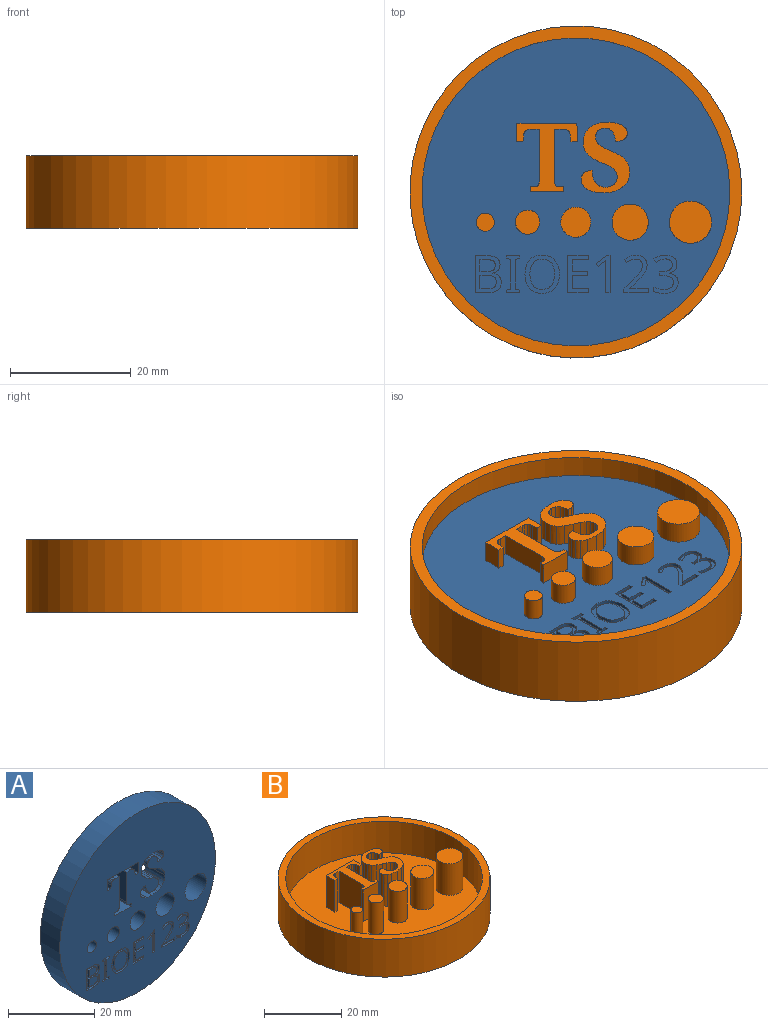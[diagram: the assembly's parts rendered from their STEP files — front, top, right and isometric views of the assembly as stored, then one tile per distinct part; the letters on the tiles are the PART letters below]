
ASSEMBLY  parts=2 mates=1
PART A: 230 faces, bbox 51x6.4x51 mm
  f0: plane 51x51mm, normal (0,-1,0), area 1751.3mm2, adj f2,f3,f4,f5,f6,f7,f8,f9
  f1: plane 51x51mm, normal (0,1,0), area 1845.5mm2, adj f2,f3,f4,f5,f6,f7,f8,f9
  f2: cylinder r=25.5mm len=51mm, axis (0,1,0), area 1017.4mm2, adj f0,f1
  f3: plane 8.53x6.35mm, normal (-1,0,0), area 54.2mm2, adj f0,f1,f4,f34
  f4: plane 6.35x1.28mm, normal (0,0,1), area 8.1mm2, adj f0,f1,f3,f5
  f5: extruded ~6.35x0.6mm, area 3.9mm2, adj f0,f1,f4,f6
  f6: extruded ~6.35x0.39mm, area 2.9mm2, adj f0,f1,f5,f7
  f7: extruded ~6.35x0.36mm, area 2.7mm2, adj f0,f1,f6,f8
  f8: extruded ~6.35x0.48mm, area 3.1mm2, adj f0,f1,f7,f9
  f9: plane 6.35x0.99mm, normal (0.99,0,0.12), area 6.3mm2, adj f0,f1,f8,f10
  f10: plane 6.35x1.07mm, normal (0,0,1), area 6.8mm2, adj f0,f1,f9,f11
  f11: plane 6.35x3.09mm, normal (-1,0,-0.03), area 19.6mm2, adj f0,f1,f10,f12
  f12: plane 9.94x6.35mm, normal (0,0,-1), area 63.1mm2, adj f0,f1,f11,f13
  f13: plane 6.35x3.09mm, normal (1,0,-0.03), area 19.6mm2, adj f0,f1,f12,f14
  f14: plane 6.35x1.07mm, normal (0,0,1), area 6.8mm2, adj f0,f1,f13,f15
  f15: plane 6.35x0.99mm, normal (-0.99,0,0.11), area 6.3mm2, adj f0,f1,f14,f16
  f16: extruded ~6.35x0.48mm, area 3.1mm2, adj f0,f1,f15,f17
  f17: extruded ~6.35x0.36mm, area 2.7mm2, adj f0,f1,f16,f18
  f18: extruded ~6.35x0.39mm, area 2.9mm2, adj f0,f1,f17,f19
  f19: extruded ~6.35x0.6mm, area 3.9mm2, adj f0,f1,f18,f20
  f20: plane 6.35x1.28mm, normal (0,0,1), area 8.1mm2, adj f0,f1,f19,f21
  f21: plane 8.53x6.35mm, normal (1,0,0), area 54.2mm2, adj f0,f1,f20,f22
  f22: extruded ~6.35x0.54mm, area 3.5mm2, adj f0,f1,f21,f23
  f23: extruded ~6.35x0.31mm, area 2.3mm2, adj f0,f1,f22,f24
  f24: extruded ~6.35x0.26mm, area 1.9mm2, adj f0,f1,f23,f25
  f25: extruded ~6.35x0.33mm, area 2.1mm2, adj f0,f1,f24,f26
  f26: plane 6.35x0.67mm, normal (0,0,-1), area 4.3mm2, adj f0,f1,f25,f27
  f27: plane 6.35x0.85mm, normal (1,0,0), area 5.4mm2, adj f0,f1,f26,f28
  f28: plane 6.35x5.51mm, normal (0,0,1), area 35mm2, adj f0,f1,f27,f29
  f29: plane 6.35x0.85mm, normal (-1,0,0), area 5.4mm2, adj f0,f1,f28,f30
  f30: plane 6.35x0.67mm, normal (0,0,-1), area 4.3mm2, adj f0,f1,f29,f31
  f31: extruded ~6.35x0.32mm, area 2mm2, adj f0,f1,f30,f32
  f32: extruded ~6.35x0.26mm, area 1.9mm2, adj f0,f1,f31,f33
  f33: extruded ~6.35x0.31mm, area 2.3mm2, adj f0,f1,f32,f34
  f34: extruded ~6.35x0.54mm, area 3.5mm2, adj f0,f1,f3,f33
  f35: extruded ~6.35x1.79mm, area 11.6mm2, adj f0,f1,f36,f90
  f36: extruded ~6.35x1.37mm, area 9.9mm2, adj f0,f1,f35,f37
  f37: extruded ~6.35x1.1mm, area 9mm2, adj f0,f1,f36,f38
  f38: extruded ~6.35x1.41mm, area 9.3mm2, adj f0,f1,f37,f39
  f39: extruded ~6.35x1.06mm, area 6.9mm2, adj f0,f1,f38,f40
  f40: extruded ~6.35x0.88mm, area 6.6mm2, adj f0,f1,f39,f41
  f41: extruded ~6.35x0.95mm, area 7.7mm2, adj f0,f1,f40,f42
  f42: extruded ~6.35x1.4mm, area 9.9mm2, adj f0,f1,f41,f43
  f43: extruded ~6.35x1.32mm, area 9.2mm2, adj f0,f1,f42,f44
  f44: extruded ~6.35x0.8mm, area 6.3mm2, adj f0,f1,f43,f45
  f45: extruded ~6.35x0.58mm, area 4.5mm2, adj f0,f1,f44,f46
  f46: extruded ~6.35x0.63mm, area 4.1mm2, adj f0,f1,f45,f47
  f47: extruded ~6.35x0.64mm, area 4.1mm2, adj f0,f1,f46,f48
  f48: extruded ~6.35x0.46mm, area 3.7mm2, adj f0,f1,f47,f49
  f49: extruded ~6.35x0.5mm, area 3.7mm2, adj f0,f1,f48,f50
  f50: extruded ~6.35x0.61mm, area 3.9mm2, adj f0,f1,f49,f51
  f51: extruded ~6.35x0.78mm, area 5.2mm2, adj f0,f1,f50,f52
  f52: extruded ~6.35x0.55mm, area 4.9mm2, adj f0,f1,f51,f53
  f53: extruded ~6.35x0.72mm, area 4.9mm2, adj f0,f1,f52,f54
  f54: extruded ~6.35x0.72mm, area 4.6mm2, adj f0,f1,f53,f55
  f55: extruded ~6.35x0.86mm, area 5.5mm2, adj f0,f1,f54,f56
  f56: extruded ~6.35x0.62mm, area 4.3mm2, adj f0,f1,f55,f57
  f57: extruded ~6.35x0.42mm, area 3.6mm2, adj f0,f1,f56,f58
  f58: extruded ~6.35x0.52mm, area 3.4mm2, adj f0,f1,f57,f59
  f59: extruded ~6.35x0.73mm, area 4.9mm2, adj f0,f1,f58,f60
  f60: extruded ~6.35x0.62mm, area 5.5mm2, adj f0,f1,f59,f61
  f61: extruded ~6.35x1.06mm, area 7.2mm2, adj f0,f1,f60,f62
  f62: extruded ~6.35x1.52mm, area 9.7mm2, adj f0,f1,f61,f63
  f63: extruded ~6.35x1.56mm, area 10mm2, adj f0,f1,f62,f64
  f64: extruded ~6.35x1.24mm, area 8.9mm2, adj f0,f1,f63,f65
  f65: extruded ~6.35x1.01mm, area 8.3mm2, adj f0,f1,f64,f66
  f66: extruded ~6.35x1.32mm, area 8.7mm2, adj f0,f1,f65,f67
  f67: extruded ~6.35x1.07mm, area 6.9mm2, adj f0,f1,f66,f68
  f68: extruded ~6.35x0.91mm, area 6.7mm2, adj f0,f1,f67,f69
  f69: extruded ~6.35x0.92mm, area 7.7mm2, adj f0,f1,f68,f70
  f70: extruded ~6.35x1.41mm, area 10mm2, adj f0,f1,f69,f71
  f71: extruded ~6.35x1.17mm, area 8.2mm2, adj f0,f1,f70,f72
  f72: extruded ~6.35x0.83mm, area 6.2mm2, adj f0,f1,f71,f73
  f73: extruded ~6.35x0.58mm, area 4.9mm2, adj f0,f1,f72,f74
  f74: extruded ~6.35x0.72mm, area 4.7mm2, adj f0,f1,f73,f75
  f75: extruded ~6.35x0.68mm, area 4.4mm2, adj f0,f1,f74,f76
  f76: extruded ~6.35x0.55mm, area 4.3mm2, adj f0,f1,f75,f77
  f77: extruded ~6.35x0.62mm, area 4.6mm2, adj f0,f1,f76,f78
  f78: extruded ~6.35x0.83mm, area 5.4mm2, adj f0,f1,f77,f79
  f79: extruded ~6.35x0.88mm, area 5.7mm2, adj f0,f1,f78,f80
  f80: extruded ~6.35x0.69mm, area 5.5mm2, adj f0,f1,f79,f81
  f81: extruded ~6.35x0.87mm, area 6.2mm2, adj f0,f1,f80,f82
  f82: extruded ~6.35x1.2mm, area 7.7mm2, adj f0,f1,f81,f83
  f83: extruded ~6.35x0.67mm, area 4.3mm2, adj f0,f1,f82,f84
  f84: extruded ~6.35x0.58mm, area 4mm2, adj f0,f1,f83,f85
  f85: extruded ~6.35x0.46mm, area 3.9mm2, adj f0,f1,f84,f86
  f86: extruded ~6.35x0.69mm, area 4.6mm2, adj f0,f1,f85,f87
  f87: extruded ~6.35x0.79mm, area 5.2mm2, adj f0,f1,f86,f88
  f88: extruded ~6.35x0.72mm, area 6.1mm2, adj f0,f1,f87,f89
  f89: extruded ~6.35x1.15mm, area 8mm2, adj f0,f1,f88,f90
  f90: extruded ~6.35x1.79mm, area 11.5mm2, adj f0,f1,f35,f89
  f91: cylinder r=3.5mm len=7mm, axis (0,-1,0), area 139.6mm2, adj f0,f1
  f92: cylinder r=3mm len=6.35mm, axis (0,-1,0), area 119.7mm2, adj f0,f1
  f93: cylinder r=1.5mm len=6.35mm, axis (0,-1,0), area 59.8mm2, adj f0,f1
  f94: cylinder r=2mm len=6.35mm, axis (0,-1,0), area 79.8mm2, adj f0,f1
  f95: cylinder r=2.5mm len=6.35mm, axis (0,-1,0), area 99.7mm2, adj f0,f1
  f96: plane 0.5x0.45mm, normal (-1,0,0), area 0.2mm2, adj f0,f97,f107,f108
  f97: plane 0.73x0.5mm, normal (-0.22,0,-0.98), area 0.4mm2, adj f0,f96,f98,f108
  f98: plane 4.94x0.5mm, normal (-1,0,0), area 2.5mm2, adj f0,f97,f99,f108
  f99: plane 0.73x0.5mm, normal (-0.23,0,0.97), area 0.4mm2, adj f0,f98,f100,f108
  f100: plane 0.5x0.45mm, normal (-1,0,0), area 0.2mm2, adj f0,f99,f101,f108
  f101: plane 2.23x0.5mm, normal (0,0,-1), area 1.1mm2, adj f0,f100,f102,f108
  f102: plane 0.5x0.45mm, normal (1,0,0), area 0.2mm2, adj f0,f101,f103,f108
  f103: plane 0.73x0.5mm, normal (0.23,0,0.97), area 0.4mm2, adj f0,f102,f104,f108
  f104: plane 4.94x0.5mm, normal (1,0,0), area 2.5mm2, adj f0,f103,f105,f108
  f105: plane 0.73x0.5mm, normal (0.22,0,-0.98), area 0.4mm2, adj f0,f104,f106,f108
  f106: plane 0.5x0.45mm, normal (1,0,0), area 0.2mm2, adj f0,f105,f107,f108
  f107: plane 2.23x0.5mm, normal (0,0,1), area 1.1mm2, adj f0,f96,f106,f108
  f108: plane 6.17x2.23mm, normal (0,-1,0), area 6.3mm2, adj f96,f97,f98,f99,f100,f101,f102,f103
  f109: plane 0.68x0.5mm, normal (-1,0,0), area 0.3mm2, adj f0,f110,f120,f121
  f110: plane 2.67x0.5mm, normal (0,0,-1), area 1.3mm2, adj f0,f109,f111,f121
  f111: plane 2.2x0.5mm, normal (-1,0,0), area 1.1mm2, adj f0,f110,f112,f121
  f112: plane 2.52x0.5mm, normal (0,0,1), area 1.3mm2, adj f0,f111,f113,f121
  f113: plane 0.68x0.5mm, normal (-1,0,0), area 0.3mm2, adj f0,f112,f114,f121
  f114: plane 2.52x0.5mm, normal (0,0,-1), area 1.3mm2, adj f0,f113,f115,f121
  f115: plane 1.92x0.5mm, normal (-1,0,0), area 1mm2, adj f0,f114,f116,f121
  f116: plane 2.67x0.5mm, normal (0,0,1), area 1.3mm2, adj f0,f115,f117,f121
  f117: plane 0.68x0.5mm, normal (-1,0,0), area 0.3mm2, adj f0,f116,f118,f121
  f118: plane 3.45x0.5mm, normal (0,0,-1), area 1.7mm2, adj f0,f117,f119,f121
  f119: plane 6.17x0.5mm, normal (1,0,0), area 3.1mm2, adj f0,f118,f120,f121
  f120: plane 3.45x0.5mm, normal (0,0,1), area 1.7mm2, adj f0,f109,f119,f121
  f121: plane 6.17x3.45mm, normal (0,-1,0), area 10.1mm2, adj f109,f110,f111,f112,f113,f114,f115,f116
  f122: plane 6.17x0.5mm, normal (-1,0,0), area 3.1mm2, adj f0,f123,f130,f131
  f123: plane 0.63x0.5mm, normal (0,0,-1), area 0.3mm2, adj f0,f122,f124,f131
  f124: plane 1.67x1.3mm, normal (0.61,0,-0.79), area 1.1mm2, adj f0,f123,f125,f131
  f125: plane 0.51x0.5mm, normal (0.79,0,0.61), area 0.3mm2, adj f0,f124,f126,f131
  f126: extruded ~0.94x0.78mm, area 0.6mm2, adj f0,f125,f127,f131
  f127: extruded ~0.5x0.25mm, area 0.2mm2, adj f0,f126,f128,f131
  f128: extruded ~1.06x0.5mm, area 0.5mm2, adj f0,f127,f129,f131
  f129: plane 4.31x0.5mm, normal (1,0,0), area 2.2mm2, adj f0,f128,f130,f131
  f130: plane 0.74x0.5mm, normal (0,0,1), area 0.4mm2, adj f0,f122,f129,f131
  f131: plane 6.17x2.3mm, normal (0,-1,0), area 5.6mm2, adj f122,f123,f124,f125,f126,f127,f128,f129
  f132: plane 0.69x0.5mm, normal (-1,0,0), area 0.3mm2, adj f0,f133,f152,f153
  f133: plane 3.12x0.5mm, normal (0,0,-1), area 1.6mm2, adj f0,f132,f134,f153
  f134: plane 0.5x0.03mm, normal (-1,0,0), area 0mm2, adj f0,f133,f135,f153
  f135: plane 1.29x1.27mm, normal (-0.7,0,0.71), area 0.9mm2, adj f0,f134,f136,f153
  f136: extruded ~1.07x0.99mm, area 0.7mm2, adj f0,f135,f137,f153
  f137: extruded ~0.77x0.5mm, area 0.4mm2, adj f0,f136,f138,f153
  f138: extruded ~0.78x0.5mm, area 0.4mm2, adj f0,f137,f139,f153
  f139: extruded ~1.2x0.5mm, area 0.7mm2, adj f0,f138,f140,f153
  f140: extruded ~1.37x0.5mm, area 0.7mm2, adj f0,f139,f141,f153
  f141: extruded ~1.89x0.73mm, area 1mm2, adj f0,f140,f142,f153
  f142: plane 0.51x0.5mm, normal (0.78,0,0.62), area 0.3mm2, adj f0,f141,f143,f153
  f143: extruded ~0.77x0.5mm, area 0.4mm2, adj f0,f142,f144,f153
  f144: extruded ~0.72x0.5mm, area 0.4mm2, adj f0,f143,f145,f153
  f145: extruded ~0.8x0.5mm, area 0.4mm2, adj f0,f144,f146,f153
  f146: extruded ~0.76x0.5mm, area 0.4mm2, adj f0,f145,f147,f153
  f147: extruded ~0.64x0.5mm, area 0.3mm2, adj f0,f146,f148,f153
  f148: extruded ~0.61x0.5mm, area 0.4mm2, adj f0,f147,f149,f153
  f149: extruded ~1.06x0.97mm, area 0.7mm2, adj f0,f148,f150,f153
  f150: plane 1.63x1.62mm, normal (0.71,0,-0.7), area 1.1mm2, adj f0,f149,f151,f153
  f151: plane 0.63x0.5mm, normal (1,0,0), area 0.3mm2, adj f0,f150,f152,f153
  f152: plane 4.08x0.5mm, normal (0,0,1), area 2mm2, adj f0,f132,f151,f153
  f153: plane 6.26x4.08mm, normal (0,-1,0), area 9mm2, adj f132,f133,f134,f135,f136,f137,f138,f139
  f154: extruded ~1.12x0.5mm, area 0.6mm2, adj f0,f155,f181,f182
  f155: extruded ~1.41x0.5mm, area 0.7mm2, adj f0,f154,f156,f182
  f156: extruded ~1.05x0.5mm, area 0.5mm2, adj f0,f155,f157,f182
  f157: extruded ~0.88x0.5mm, area 0.5mm2, adj f0,f156,f158,f182
  f158: plane 0.52x0.5mm, normal (0.81,0,0.59), area 0.3mm2, adj f0,f157,f159,f182
  f159: extruded ~0.8x0.5mm, area 0.4mm2, adj f0,f158,f160,f182
  f160: extruded ~0.76x0.5mm, area 0.4mm2, adj f0,f159,f161,f182
  f161: extruded ~0.83x0.5mm, area 0.4mm2, adj f0,f160,f162,f182
  f162: extruded ~0.69x0.5mm, area 0.4mm2, adj f0,f161,f163,f182
  f163: extruded ~0.86x0.5mm, area 0.5mm2, adj f0,f162,f164,f182
  f164: extruded ~1.14x0.5mm, area 0.6mm2, adj f0,f163,f165,f182
  f165: plane 0.61x0.5mm, normal (0,0,-1), area 0.3mm2, adj f0,f164,f166,f182
  f166: plane 0.65x0.5mm, normal (1,0,0), area 0.3mm2, adj f0,f165,f167,f182
  f167: plane 0.6x0.5mm, normal (0,0,1), area 0.3mm2, adj f0,f166,f168,f182
  f168: extruded ~1.73x1.09mm, area 1.2mm2, adj f0,f167,f169,f182
  f169: extruded ~1.56x1.22mm, area 1.1mm2, adj f0,f168,f170,f182
  f170: extruded ~0.87x0.5mm, area 0.4mm2, adj f0,f169,f171,f182
  f171: extruded ~0.84x0.5mm, area 0.4mm2, adj f0,f170,f172,f182
  f172: plane 0.71x0.5mm, normal (1,0,0), area 0.4mm2, adj f0,f171,f173,f182
  f173: extruded ~0.8x0.5mm, area 0.4mm2, adj f0,f172,f174,f182
  f174: extruded ~0.9x0.5mm, area 0.5mm2, adj f0,f173,f175,f182
  f175: extruded ~1.76x0.5mm, area 0.9mm2, adj f0,f174,f176,f182
  f176: extruded ~1.36x0.61mm, area 0.8mm2, adj f0,f175,f177,f182
  f177: extruded ~0.99x0.5mm, area 0.5mm2, adj f0,f176,f178,f182
  f178: extruded ~1.1x0.5mm, area 0.6mm2, adj f0,f177,f179,f182
  f179: plane 0.5x0.03mm, normal (-1,0,0), area 0mm2, adj f0,f178,f180,f182
  f180: extruded ~0.95x0.51mm, area 0.5mm2, adj f0,f179,f181,f182
  f181: extruded ~0.97x0.5mm, area 0.5mm2, adj f0,f154,f180,f182
  f182: plane 6.34x4.06mm, normal (0,-1,0), area 9.5mm2, adj f154,f155,f156,f157,f158,f159,f160,f161
  f183: extruded ~2.33x0.75mm, area 1.3mm2, adj f0,f184,f198,f199
  f184: extruded ~2.09x0.84mm, area 1.2mm2, adj f0,f183,f185,f199
  f185: extruded ~2.12x0.83mm, area 1.2mm2, adj f0,f184,f186,f199
  f186: extruded ~2.34x0.74mm, area 1.3mm2, adj f0,f185,f187,f199
  f187: extruded ~2.35x0.75mm, area 1.3mm2, adj f0,f186,f188,f199
  f188: extruded ~2.11x0.83mm, area 1.2mm2, adj f0,f187,f189,f199
  f189: extruded ~2.1x0.85mm, area 1.2mm2, adj f0,f188,f198,f199
  f190: extruded ~1.85x0.52mm, area 1mm2, adj f191,f197,f199,f200
  f191: extruded ~1.52x0.63mm, area 0.9mm2, adj f190,f192,f199,f200
  f192: extruded ~1.5x0.63mm, area 0.8mm2, adj f191,f193,f199,f200
  f193: extruded ~1.86x0.51mm, area 1mm2, adj f192,f194,f199,f200
  f194: extruded ~1.87x0.51mm, area 1mm2, adj f193,f195,f199,f200
  f195: extruded ~1.51x0.63mm, area 0.8mm2, adj f194,f196,f199,f200
  f196: extruded ~1.51x0.64mm, area 0.9mm2, adj f195,f197,f199,f200
  f197: extruded ~1.87x0.52mm, area 1mm2, adj f190,f196,f199,f200
  f198: extruded ~2.33x0.75mm, area 1.3mm2, adj f0,f183,f189,f199
  f199: plane 6.35x5.7mm, normal (0,-1,0), area 12.9mm2, adj f183,f184,f185,f186,f187,f188,f189,f190
  f200: plane 5x4.06mm, normal (0,-1,0), area 16.8mm2, adj f190,f191,f192,f193,f194,f195,f196,f197
  f201: plane 6.17x0.5mm, normal (1,0,0), area 3.1mm2, adj f0,f202,f226,f227
  f202: plane 2.17x0.5mm, normal (0,0,1), area 1.1mm2, adj f0,f201,f203,f227
  f203: extruded ~1.58x0.5mm, area 0.8mm2, adj f0,f202,f204,f227
  f204: extruded ~1.29x0.57mm, area 0.7mm2, adj f0,f203,f205,f227
  f205: extruded ~0.98x0.5mm, area 0.5mm2, adj f0,f204,f206,f227
  f206: extruded ~1.05x0.5mm, area 0.6mm2, adj f0,f205,f207,f227
  f207: plane 0.5x0.04mm, normal (-1,0,0), area 0mm2, adj f0,f206,f208,f227
  f208: extruded ~0.87x0.5mm, area 0.5mm2, adj f0,f207,f209,f227
  f209: extruded ~0.91x0.5mm, area 0.5mm2, adj f0,f208,f210,f227
  f210: extruded ~1.16x0.55mm, area 0.7mm2, adj f0,f209,f211,f227
  f211: extruded ~1.79x0.5mm, area 0.9mm2, adj f0,f210,f226,f227
  f212: plane 1.96x0.5mm, normal (-1,0,0), area 1mm2, adj f213,f224,f227,f229
  f213: plane 1.02x0.5mm, normal (0,0,1), area 0.5mm2, adj f212,f214,f227,f229
  f214: extruded ~1.14x0.5mm, area 0.6mm2, adj f213,f215,f227,f229
  f215: extruded ~0.73x0.5mm, area 0.4mm2, adj f214,f216,f227,f229
  f216: extruded ~0.78x0.5mm, area 0.4mm2, adj f215,f217,f227,f229
  f217: extruded ~1.06x0.5mm, area 0.5mm2, adj f216,f224,f227,f229
  f218: plane 1.19x0.5mm, normal (0,0,1), area 0.6mm2, adj f219,f225,f227,f228
  f219: extruded ~1.14x0.5mm, area 0.6mm2, adj f218,f220,f227,f228
  f220: extruded ~0.82x0.5mm, area 0.5mm2, adj f219,f221,f227,f228
  f221: extruded ~0.87x0.5mm, area 0.5mm2, adj f220,f222,f227,f228
  f222: extruded ~1.1x0.5mm, area 0.6mm2, adj f221,f223,f227,f228
  f223: plane 1.25x0.5mm, normal (0,0,-1), area 0.6mm2, adj f222,f225,f227,f228
  f224: plane 1.14x0.5mm, normal (0,0,-1), area 0.6mm2, adj f212,f217,f227,f229
  f225: plane 2.24x0.5mm, normal (-1,0,0), area 1.1mm2, adj f218,f223,f227,f228
  f226: plane 1.76x0.5mm, normal (0,0,-1), area 0.9mm2, adj f0,f201,f211,f227
  f227: plane 6.17x4.31mm, normal (0,-1,0), area 13.9mm2, adj f201,f202,f203,f204,f205,f206,f207,f208
  f228: plane 2.71x2.24mm, normal (0,-1,0), area 5.5mm2, adj f218,f219,f220,f221,f222,f223,f225
  f229: plane 2.52x1.96mm, normal (0,-1,0), area 4.5mm2, adj f212,f213,f214,f215,f216,f217,f224
PART B: 105 faces, bbox 55x55x12 mm
  f0: plane 51x51mm, normal (0,0,1), area 1845.5mm2, adj f4,f5,f6,f7,f8,f9,f10,f11
  f1: plane 55x55mm, normal (0,0,-1), area 2375.8mm2, adj f2
  f2: cylinder r=27.5mm len=55mm, axis (0,0,1), area 2073.5mm2, adj f1,f3
  f3: plane 55x55mm, normal (0,0,1), area 333mm2, adj f2,f4
  f4: cylinder r=25.5mm len=51mm, axis (0,0,1), area 1602.2mm2, adj f0,f3
  f5: plane 10x8.53mm, normal (1,0,0), area 85.3mm2, adj f0,f6,f36,f37
  f6: plane 10x1.28mm, normal (0,-1,0), area 12.8mm2, adj f0,f5,f7,f37
  f7: extruded ~10x0.6mm, area 6.1mm2, adj f0,f6,f8,f37
  f8: extruded ~10x0.39mm, area 4.6mm2, adj f0,f7,f9,f37
  f9: extruded ~10x0.36mm, area 4.2mm2, adj f0,f8,f10,f37
  f10: extruded ~10x0.48mm, area 4.9mm2, adj f0,f9,f11,f37
  f11: plane 10x0.99mm, normal (-0.99,-0.12,0), area 10mm2, adj f0,f10,f12,f37
  f12: plane 10x1.07mm, normal (0,-1,0), area 10.7mm2, adj f0,f11,f13,f37
  f13: plane 10x3.09mm, normal (1,0.03,0), area 30.9mm2, adj f0,f12,f14,f37
  f14: plane 10x9.94mm, normal (0,1,0), area 99.4mm2, adj f0,f13,f15,f37
  f15: plane 10x3.09mm, normal (-1,0.03,0), area 30.9mm2, adj f0,f14,f16,f37
  f16: plane 10x1.07mm, normal (0,-1,0), area 10.7mm2, adj f0,f15,f17,f37
  f17: plane 10x0.99mm, normal (0.99,-0.11,0), area 10mm2, adj f0,f16,f18,f37
  f18: extruded ~10x0.48mm, area 4.9mm2, adj f0,f17,f19,f37
  f19: extruded ~10x0.36mm, area 4.2mm2, adj f0,f18,f20,f37
  f20: extruded ~10x0.39mm, area 4.6mm2, adj f0,f19,f21,f37
  f21: extruded ~10x0.6mm, area 6.1mm2, adj f0,f20,f22,f37
  f22: plane 10x1.28mm, normal (0,-1,0), area 12.8mm2, adj f0,f21,f23,f37
  f23: plane 10x8.53mm, normal (-1,0,0), area 85.3mm2, adj f0,f22,f24,f37
  f24: extruded ~10x0.54mm, area 5.5mm2, adj f0,f23,f25,f37
  f25: extruded ~10x0.31mm, area 3.6mm2, adj f0,f24,f26,f37
  f26: extruded ~10x0.26mm, area 3mm2, adj f0,f25,f27,f37
  f27: extruded ~10x0.33mm, area 3.3mm2, adj f0,f26,f28,f37
  f28: plane 10x0.67mm, normal (0,1,0), area 6.7mm2, adj f0,f27,f29,f37
  f29: plane 10x0.85mm, normal (-1,0,0), area 8.5mm2, adj f0,f28,f30,f37
  f30: plane 10x5.51mm, normal (0,-1,0), area 55.1mm2, adj f0,f29,f31,f37
  f31: plane 10x0.85mm, normal (1,0,0), area 8.5mm2, adj f0,f30,f32,f37
  f32: plane 10x0.67mm, normal (0,1,0), area 6.7mm2, adj f0,f31,f33,f37
  f33: extruded ~10x0.32mm, area 3.2mm2, adj f0,f32,f34,f37
  f34: extruded ~10x0.26mm, area 3mm2, adj f0,f33,f35,f37
  f35: extruded ~10x0.31mm, area 3.6mm2, adj f0,f34,f36,f37
  f36: extruded ~10x0.54mm, area 5.5mm2, adj f0,f5,f35,f37
  f37: plane 11.39x10.1mm, normal (0,0,1), area 44.2mm2, adj f5,f6,f7,f8,f9,f10,f11,f12
  f38: extruded ~10x1.79mm, area 18.2mm2, adj f0,f39,f93,f94
  f39: extruded ~10x1.37mm, area 15.5mm2, adj f0,f38,f40,f94
  f40: extruded ~10x1.1mm, area 14.2mm2, adj f0,f39,f41,f94
  f41: extruded ~10x1.41mm, area 14.6mm2, adj f0,f40,f42,f94
  f42: extruded ~10x1.06mm, area 10.8mm2, adj f0,f41,f43,f94
  f43: extruded ~10x0.88mm, area 10.4mm2, adj f0,f42,f44,f94
  f44: extruded ~10x0.95mm, area 12.1mm2, adj f0,f43,f45,f94
  f45: extruded ~10x1.4mm, area 15.6mm2, adj f0,f44,f46,f94
  f46: extruded ~10x1.32mm, area 14.6mm2, adj f0,f45,f47,f94
  f47: extruded ~10x0.8mm, area 9.9mm2, adj f0,f46,f48,f94
  f48: extruded ~10x0.58mm, area 7.1mm2, adj f0,f47,f49,f94
  f49: extruded ~10x0.63mm, area 6.4mm2, adj f0,f48,f50,f94
  f50: extruded ~10x0.64mm, area 6.5mm2, adj f0,f49,f51,f94
  f51: extruded ~10x0.46mm, area 5.8mm2, adj f0,f50,f52,f94
  f52: extruded ~10x0.5mm, area 5.8mm2, adj f0,f51,f53,f94
  f53: extruded ~10x0.61mm, area 6.2mm2, adj f0,f52,f54,f94
  f54: extruded ~10x0.78mm, area 8.3mm2, adj f0,f53,f55,f94
  f55: extruded ~10x0.55mm, area 7.7mm2, adj f0,f54,f56,f94
  f56: extruded ~10x0.72mm, area 7.8mm2, adj f0,f55,f57,f94
  f57: extruded ~10x0.72mm, area 7.3mm2, adj f0,f56,f58,f94
  f58: extruded ~10x0.86mm, area 8.7mm2, adj f0,f57,f59,f94
  f59: extruded ~10x0.62mm, area 6.8mm2, adj f0,f58,f60,f94
  f60: extruded ~10x0.42mm, area 5.6mm2, adj f0,f59,f61,f94
  f61: extruded ~10x0.52mm, area 5.4mm2, adj f0,f60,f62,f94
  f62: extruded ~10x0.73mm, area 7.6mm2, adj f0,f61,f63,f94
  f63: extruded ~10x0.62mm, area 8.6mm2, adj f0,f62,f64,f94
  f64: extruded ~10x1.06mm, area 11.3mm2, adj f0,f63,f65,f94
  f65: extruded ~10x1.52mm, area 15.3mm2, adj f0,f64,f66,f94
  f66: extruded ~10x1.56mm, area 15.8mm2, adj f0,f65,f67,f94
  f67: extruded ~10x1.24mm, area 14.1mm2, adj f0,f66,f68,f94
  f68: extruded ~10x1.01mm, area 13.1mm2, adj f0,f67,f69,f94
  f69: extruded ~10x1.32mm, area 13.7mm2, adj f0,f68,f70,f94
  f70: extruded ~10x1.07mm, area 10.9mm2, adj f0,f69,f71,f94
  f71: extruded ~10x0.91mm, area 10.5mm2, adj f0,f70,f72,f94
  f72: extruded ~10x0.92mm, area 12.1mm2, adj f0,f71,f73,f94
  f73: extruded ~10x1.41mm, area 15.8mm2, adj f0,f72,f74,f94
  f74: extruded ~10x1.17mm, area 12.8mm2, adj f0,f73,f75,f94
  f75: extruded ~10x0.83mm, area 9.8mm2, adj f0,f74,f76,f94
  f76: extruded ~10x0.58mm, area 7.7mm2, adj f0,f75,f77,f94
  f77: extruded ~10x0.72mm, area 7.4mm2, adj f0,f76,f78,f94
  f78: extruded ~10x0.68mm, area 7mm2, adj f0,f77,f79,f94
  f79: extruded ~10x0.55mm, area 6.8mm2, adj f0,f78,f80,f94
  f80: extruded ~10x0.62mm, area 7.3mm2, adj f0,f79,f81,f94
  f81: extruded ~10x0.83mm, area 8.5mm2, adj f0,f80,f82,f94
  f82: extruded ~10x0.88mm, area 9mm2, adj f0,f81,f83,f94
  f83: extruded ~10x0.69mm, area 8.7mm2, adj f0,f82,f84,f94
  f84: extruded ~10x0.87mm, area 9.8mm2, adj f0,f83,f85,f94
  f85: extruded ~10x1.2mm, area 12.2mm2, adj f0,f84,f86,f94
  f86: extruded ~10x0.67mm, area 6.8mm2, adj f0,f85,f87,f94
  f87: extruded ~10x0.58mm, area 6.3mm2, adj f0,f86,f88,f94
  f88: extruded ~10x0.46mm, area 6.2mm2, adj f0,f87,f89,f94
  f89: extruded ~10x0.69mm, area 7.2mm2, adj f0,f88,f90,f94
  f90: extruded ~10x0.79mm, area 8.1mm2, adj f0,f89,f91,f94
  f91: extruded ~10x0.72mm, area 9.5mm2, adj f0,f90,f92,f94
  f92: extruded ~10x1.15mm, area 12.7mm2, adj f0,f91,f93,f94
  f93: extruded ~10x1.79mm, area 18.1mm2, adj f0,f38,f92,f94
  f94: plane 11.71x8.08mm, normal (0,0,1), area 47.1mm2, adj f38,f39,f40,f41,f42,f43,f44,f45
  f95: cylinder r=2.5mm len=10mm, axis (0,0,-1), area 157.1mm2, adj f0,f96
  f96: plane 5x5mm, normal (0,0,1), area 19.6mm2, adj f95
  f97: cylinder r=3mm len=10mm, axis (0,0,-1), area 188.5mm2, adj f0,f98
  f98: plane 6x6mm, normal (0,0,1), area 28.3mm2, adj f97
  f99: cylinder r=3.5mm len=10mm, axis (0,0,-1), area 219.9mm2, adj f0,f100
  f100: plane 7x7mm, normal (0,0,1), area 38.5mm2, adj f99
  f101: cylinder r=1.5mm len=10mm, axis (0,0,-1), area 94.2mm2, adj f0,f102
  f102: plane 3x3mm, normal (0,0,1), area 7.1mm2, adj f101
  f103: cylinder r=2mm len=10mm, axis (0,0,-1), area 125.7mm2, adj f0,f104
  f104: plane 4x4mm, normal (0,0,1), area 12.6mm2, adj f103
PLACE A rot(axis=(-1,0,0),90deg) t=(-38.71,-60.35,17.73)mm
PLACE B t=(-38.71,-60.35,15.73)mm
MATE fastened B.f0 <-> A.f1  axis (0,0,1) through (-39.15,-60.37,17.73)mm
